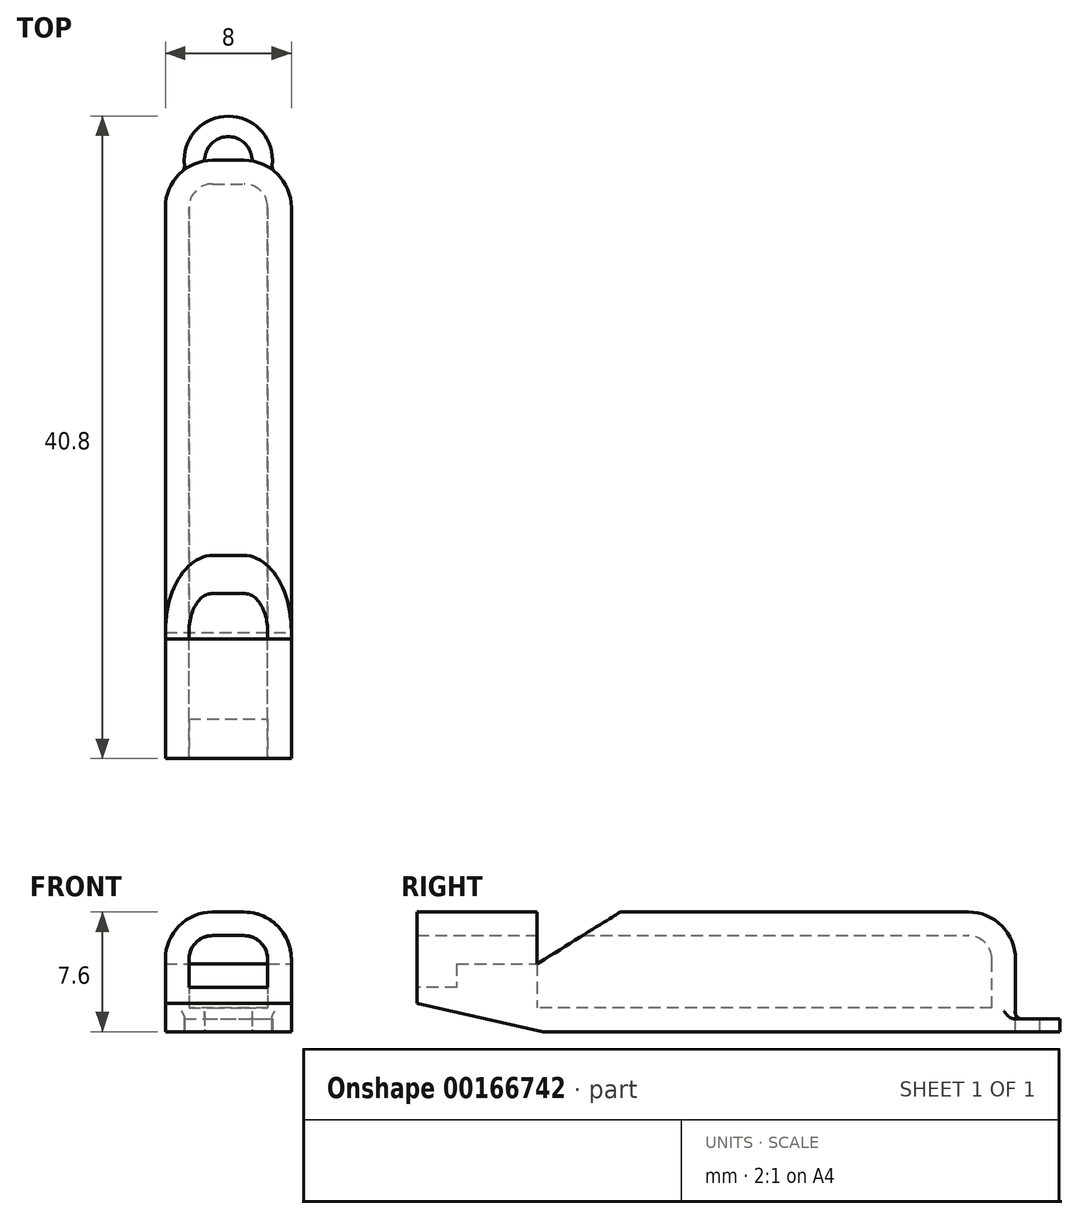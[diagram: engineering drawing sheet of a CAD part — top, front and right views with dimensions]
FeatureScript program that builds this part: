
annotation { "Feature Type Name" : "Feature", "Feature Type Description" : "" }
export const myFeature = defineFeature(function(context is Context, id is Id, definition is map)
    precondition{}
    {
        {
            var Q0;
            Q0=qCreatedBy(makeId("Front.planeOp"),FACE);
            var sketch = newSketch(context, id + "F0", { "sketchPlane" : qUnion([Q0])});
            skLineSegment(sketch, "E0.bottom", {"start": v(-4, 0) * mm, "end": v(4, 0) * mm});
            skLineSegment(sketch, "E0.top", {"start": v(-4, 7.6) * mm, "end": v(4, 7.6) * mm});
            skLineSegment(sketch, "E0.left", {"start": v(-4, 0) * mm, "end": v(-4, 7.6) * mm});
            skLineSegment(sketch, "E0.right", {"start": v(4, 0) * mm, "end": v(4, 7.6) * mm});
            skSolve(sketch);
        }
        {
            var Q0;
            Q0 = qSketchRegion(id + "F0", true);
            extrude(context, id + "F1", {"entities" : qUnion([Q0]), "oppositeDirection" : true, "depth" : 38 * mm});
        }
        {
            var Q0;
            Q0=makeQuery(id+"F1.opExtrude","SWEPT_EDGE",EDGE,{"disambiguationData":[OSD([sQuery(id+"F0.wireOp",EDGE,"E0.top"),sQuery(id+"F0.wireOp",EDGE,"E0.right")])]});
            var Q1;
            Q1=makeQuery(id+"F1.opExtrude","SWEPT_EDGE",EDGE,{"disambiguationData":[OSD([sQuery(id+"F0.wireOp",EDGE,"E0.top"),sQuery(id+"F0.wireOp",EDGE,"E0.left")])]});
            fillet(context, id + "F2", {"entities" : qUnion([Q0, Q1]), "radius" : 3 * mm, "tangentPropagation" : true, "allowEdgeOverflow" : false});
        }
        {
            var Q0;
            Q0=makeQuery(id+"F1.opExtrude","CAP_EDGE",EDGE,{"disambiguationData":[OSD([sQuery(id+"F0.wireOp",EDGE,"E0.right")])],"isStart":false});
            fillet(context, id + "F3", {"entities" : qUnion([Q0]), "radius" : 3 * mm, "tangentPropagation" : true, "allowEdgeOverflow" : false});
        }
        {
            var Q0;
            Q0=makeQuery(id+"F1.opExtrude","CAP_FACE",FACE,{"disambiguationData":[OSD([sQuery(id+"F0.wireOp",EDGE,"E0.bottom"),sQuery(id+"F0.wireOp",EDGE,"E0.top"),sQuery(id+"F0.wireOp",EDGE,"E0.left"),sQuery(id+"F0.wireOp",EDGE,"E0.right")])],"isStart":true});
            shell(context, id + "F4", {"entities" : qUnion([Q0]), "thickness" : 1.5 * mm});
        }
        {
            var Q0;
            Q0=makeQuery(id+"F1.opExtrude","CAP_FACE",FACE,{"disambiguationData":[OSD([sQuery(id+"F0.wireOp",EDGE,"E0.bottom"),sQuery(id+"F0.wireOp",EDGE,"E0.top"),sQuery(id+"F0.wireOp",EDGE,"E0.left"),sQuery(id+"F0.wireOp",EDGE,"E0.right")])],"isStart":true});
            var sketch = newSketch(context, id + "F5", { "sketchPlane" : qUnion([Q0])});
            skLineSegment(sketch, "E1.bottom", {"start": v(-4, 0) * mm, "end": v(4, 0) * mm});
            skLineSegment(sketch, "E1.top", {"start": v(-4, 4.3) * mm, "end": v(4, 4.3) * mm});
            skLineSegment(sketch, "E1.left", {"start": v(-4, 0) * mm, "end": v(-4, 4.3) * mm});
            skLineSegment(sketch, "E1.right", {"start": v(4, 0) * mm, "end": v(4, 4.3) * mm});
            skSolve(sketch);
        }
        {
            var Q0;
            Q0 = qSketchRegion(id + "F5", true);
            extrude(context, id + "F6", {"entities" : qUnion([Q0]), "operationType" : NewBodyOperationType.ADD, "oppositeDirection" : true, "depth" : 7.6 * mm});
        }
        {
            var Q0;
            Q0=makeQuery(id+"F1.opExtrude","SWEPT_FACE",FACE,{"disambiguationData":[OSD([sQuery(id+"F0.wireOp",EDGE,"E0.right")])]});
            var sketch = newSketch(context, id + "F7", { "sketchPlane" : qUnion([Q0])});
            skLineSegment(sketch, "E2.0", {"start": v(0, 4.3) * mm, "end": v(7.6, 4.3) * mm, "construction": true});
            skLineSegment(sketch, "E3.0", {"start": v(0, 7.6) * mm, "end": v(35, 7.6) * mm, "construction": true});
            skLineSegment(sketch, "E4", {"start": v(7.6, 4.3) * mm, "end": v(7.6, 7.6) * mm});
            skLineSegment(sketch, "E5", {"start": v(7.6, 7.6) * mm, "end": v(12.9, 7.6) * mm});
            skLineSegment(sketch, "E6", {"start": v(12.9, 7.6) * mm, "end": v(7.6, 4.3) * mm});
            skSolve(sketch);
        }
        {
            var Q0;
            Q0 = qSketchRegion(id + "F7", true);
            extrude(context, id + "F8", {"entities" : qUnion([Q0]), "operationType" : NewBodyOperationType.REMOVE, "endBound" : BoundingType.THROUGH_ALL, "oppositeDirection" : true, "depth" : 25 * mm});
        }
        {
            var Q0;
            Q0=makeQuery(id+"F6.boolean.opBoolean","MERGE",FACE,{"derivedFrom":[makeQuery(id+"F1.opExtrude","CAP_FACE",FACE,{"disambiguationData":[OSD([sQuery(id+"F0.wireOp",EDGE,"E0.bottom"),sQuery(id+"F0.wireOp",EDGE,"E0.top"),sQuery(id+"F0.wireOp",EDGE,"E0.left"),sQuery(id+"F0.wireOp",EDGE,"E0.right")])],"isStart":true}),makeQuery(id+"F6.opExtrude","CAP_FACE",FACE,{"disambiguationData":[OSD([sQuery(id+"F5.wireOp",EDGE,"E1.bottom"),sQuery(id+"F5.wireOp",EDGE,"E1.top"),sQuery(id+"F5.wireOp",EDGE,"E1.left"),sQuery(id+"F5.wireOp",EDGE,"E1.right")])],"isStart":true})]});
            var sketch = newSketch(context, id + "F9", { "sketchPlane" : qUnion([Q0])});
            skLineSegment(sketch, "E7.bottom", {"start": v(-2.5, 4.3) * mm, "end": v(2.5, 4.3) * mm});
            skLineSegment(sketch, "E7.top", {"start": v(-2.5, 2.8) * mm, "end": v(2.5, 2.8) * mm});
            skLineSegment(sketch, "E7.left", {"start": v(-2.5, 4.3) * mm, "end": v(-2.5, 2.8) * mm});
            skLineSegment(sketch, "E7.right", {"start": v(2.5, 4.3) * mm, "end": v(2.5, 2.8) * mm});
            skSolve(sketch);
        }
        {
            var Q0;
            Q0 = qSketchRegion(id + "F9", true);
            extrude(context, id + "F10", {"entities" : qUnion([Q0]), "operationType" : NewBodyOperationType.REMOVE, "oppositeDirection" : true, "depth" : 2.5 * mm});
        }
        {
            var Q0;
            Q0=makeQuery(id+"F1.opExtrude","SWEPT_FACE",FACE,{"disambiguationData":[OSD([sQuery(id+"F0.wireOp",EDGE,"E0.right")])]});
            var sketch = newSketch(context, id + "F11", { "sketchPlane" : qUnion([Q0])});
            skLineSegment(sketch, "E8.0", {"start": v(0, 2.8) * mm, "end": v(0, 4.6) * mm, "construction": true});
            skLineSegment(sketch, "E9", {"start": v(0, 1.8) * mm, "end": v(8, 0) * mm});
            skLineSegment(sketch, "E10", {"start": v(8, 0) * mm, "end": v(0, 0) * mm});
            skLineSegment(sketch, "E11", {"start": v(0, 0) * mm, "end": v(0, 1.8) * mm});
            skSolve(sketch);
        }
        {
            var Q0;
            Q0 = qSketchRegion(id + "F11", true);
            extrude(context, id + "F12", {"entities" : qUnion([Q0]), "operationType" : NewBodyOperationType.REMOVE, "oppositeDirection" : true, "depth" : 25 * mm});
        }
        {
            var Q0;
            Q0=makeQuery(id+"F1.opExtrude","CAP_FACE",FACE,{"disambiguationData":[OSD([sQuery(id+"F0.wireOp",EDGE,"E0.bottom"),sQuery(id+"F0.wireOp",EDGE,"E0.top"),sQuery(id+"F0.wireOp",EDGE,"E0.left"),sQuery(id+"F0.wireOp",EDGE,"E0.right")])],"isStart":false});
            var sketch = newSketch(context, id + "F13", { "sketchPlane" : qUnion([Q0])});
            skLineSegment(sketch, "E12", {"start": v(0, 0) * mm, "end": v(0, 4.6) * mm});
            skSolve(sketch);
        }
        {
            var Q0;
            Q0=qCreatedBy(makeId("Right.planeOp"),FACE);
            var sketch = newSketch(context, id + "F14", { "sketchPlane" : qUnion([Q0])});
            skLineSegment(sketch, "E13.bottom", {"start": v(39.5, 0) * mm, "end": v(40.8, 0) * mm});
            skLineSegment(sketch, "E13.top", {"start": v(39.5, 0.8) * mm, "end": v(40.8, 0.8) * mm});
            skLineSegment(sketch, "E13.left", {"start": v(39.5, 0) * mm, "end": v(39.5, 0.8) * mm});
            skLineSegment(sketch, "E13.right", {"start": v(40.8, 0) * mm, "end": v(40.8, 0.8) * mm});
            skSolve(sketch);
        }
        {
            var Q0;
            Q0 = qSketchRegion(id + "F14", true);
            var Q1;
            Q1=sQuery(id+"F13.wireOp",EDGE,"E12");
            revolve(context, id + "F15", {"operationType" : NewBodyOperationType.ADD, "entities" : qUnion([Q0]), "axis" : qUnion([Q1]), "revolveType" : RevolveType.FULL});
        }
        {
            var Q0;
            Q0=makeQuery(id+"F15.boolean.opBoolean","INTERSECT",EDGE,{"derivedFrom":[makeQuery(id+"F3.opFillet","BLEND_FACE",FACE,{"disambiguationData":[OSD([sQuery(id+"F0.wireOp",EDGE,"E0.right")])]}),makeQuery(id+"F15.opRevolve","SWEPT_FACE",FACE,{"disambiguationData":[OSD([sQuery(id+"F14.wireOp",EDGE,"E13.top")])]})]});
            var Q1;
            Q1=makeQuery(id+"F15.boolean.opBoolean","INTERSECT",EDGE,{"derivedFrom":[makeQuery(id+"F3.opFillet","BLEND_FACE",FACE,{"disambiguationData":[OSD([sQuery(id+"F0.wireOp",EDGE,"E0.left")])]}),makeQuery(id+"F15.opRevolve","SWEPT_FACE",FACE,{"disambiguationData":[OSD([sQuery(id+"F14.wireOp",EDGE,"E13.top")])]})]});
            var Q2;
            Q2=makeQuery(id+"F15.boolean.opBoolean","INTERSECT",EDGE,{"derivedFrom":[makeQuery(id+"F3.opFillet","BLEND_FACE",FACE,{"disambiguationData":[OSD([sQuery(id+"F0.wireOp",EDGE,"E0.right")])]}),makeQuery(id+"F15.opRevolve","SWEPT_FACE",FACE,{"disambiguationData":[OSD([sQuery(id+"F14.wireOp",EDGE,"E13.right")])]})]});
            var Q3;
            Q3=makeQuery(id+"F15.boolean.opBoolean","INTERSECT",EDGE,{"derivedFrom":[makeQuery(id+"F3.opFillet","BLEND_FACE",FACE,{"disambiguationData":[OSD([sQuery(id+"F0.wireOp",EDGE,"E0.left")])]}),makeQuery(id+"F15.opRevolve","SWEPT_FACE",FACE,{"disambiguationData":[OSD([sQuery(id+"F14.wireOp",EDGE,"E13.right")])]})]});
            fillet(context, id + "F16", {"entities" : qUnion([Q0, Q1, Q2, Q3]), "radius" : 0.5 * mm, "tangentPropagation" : true, "allowEdgeOverflow" : false});
        }
    });
